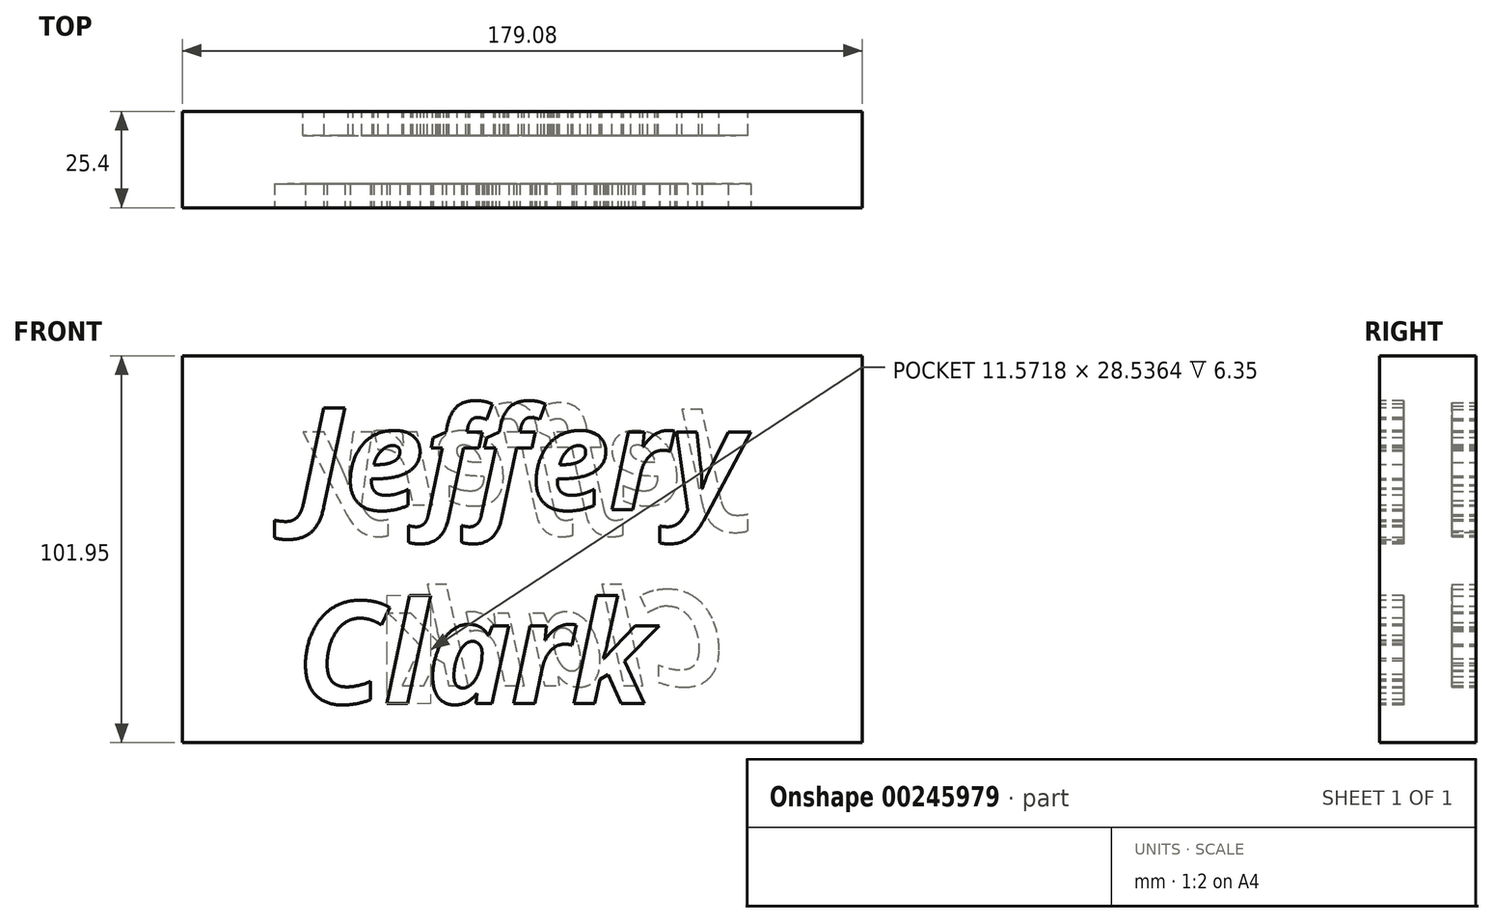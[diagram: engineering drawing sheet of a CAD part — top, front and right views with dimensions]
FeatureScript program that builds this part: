
annotation { "Feature Type Name" : "Feature", "Feature Type Description" : "" }
export const myFeature = defineFeature(function(context is Context, id is Id, definition is map)
    precondition{}
    {
        {
            var Q0;
            Q0=qCreatedBy(makeId("Front.planeOp"),FACE);
            var sketch = newSketch(context, id + "F0", { "sketchPlane" : qUnion([Q0])});
            skLineSegment(sketch, "E0.bottom", {"start": v(-67.38, 41.89) * mm, "end": v(111.7, 41.89) * mm});
            skLineSegment(sketch, "E0.top", {"start": v(-67.38, -60.06) * mm, "end": v(111.7, -60.06) * mm});
            skLineSegment(sketch, "E0.left", {"start": v(-67.38, 41.89) * mm, "end": v(-67.38, -60.06) * mm});
            skLineSegment(sketch, "E0.right", {"start": v(111.7, 41.89) * mm, "end": v(111.7, -60.06) * mm});
            skLineSegment(sketch, "E1.bottom", {"start": v(-3.55, 41.89) * mm, "end": v(-18.62, 41.89) * mm});
            skLineSegment(sketch, "E1.top", {"start": v(-3.55, 41.89) * mm, "end": v(-18.62, 41.89) * mm});
            skLineSegment(sketch, "E1.left", {"start": v(-3.55, 41.89) * mm, "end": v(-3.55, 41.89) * mm});
            skLineSegment(sketch, "E1.right", {"start": v(-18.62, 41.89) * mm, "end": v(-18.62, 41.89) * mm});
            skLineSegment(sketch, "E2.bottom", {"start": v(-67.38, 41.89) * mm, "end": v(-67.38, 41.89) * mm});
            skLineSegment(sketch, "E2.top", {"start": v(-67.38, -60.06) * mm, "end": v(-67.38, -60.06) * mm});
            skSolve(sketch);
        }
        {
            var Q0;
            Q0=makeQuery(id+"F0.imprint","IMPRINT",FACE,{"disambiguationData":[TD([[makeQuery(id+"F0.imprint","IMPRINT",EDGE,{"derivedFrom":sQuery(id+"F0.wireOp",EDGE,"E0.top")}),1.0]])]});
            extrude(context, id + "F1", {"entities" : qUnion([Q0]), "depth" : 25.4 * mm});
        }
        {
            var Q0;
            Q0=makeQuery(id+"F1.opExtrude","CAP_FACE",FACE,{"disambiguationData":[OSD([sQuery(id+"F0.wireOp",EDGE,"E0.bottom"),sQuery(id+"F0.wireOp",EDGE,"E0.top"),sQuery(id+"F0.wireOp",EDGE,"E0.right"),sQuery(id+"F0.wireOp",EDGE,"E1.top"),sQuery(id+"F0.wireOp",EDGE,"E0.left")])],"isStart":false});
            var sketch = newSketch(context, id + "F2", { "sketchPlane" : qUnion([Q0])});
            skText(sketch, "E3", { "text": "Jeffery\nClark", "fontName": "OpenSans-BoldItalic.ttf"});
            const initialGuessF2  = {"E3": [-0.03723, 0.00133, 1, 0, 0.02704]};
            skSetInitialGuess(sketch, initialGuessF2);
            skSolve(sketch);
        }
        {
            var Q0;
            Q0 = qSketchRegion(id + "F2", true);
            extrude(context, id + "F3", {"entities" : qUnion([Q0]), "operationType" : NewBodyOperationType.REMOVE, "oppositeDirection" : true, "depth" : 6.35 * mm});
        }
        {
            var Q0;
            Q0=makeQuery(id+"F1.opExtrude","CAP_FACE",FACE,{"disambiguationData":[OSD([sQuery(id+"F0.wireOp",EDGE,"E0.bottom"),sQuery(id+"F0.wireOp",EDGE,"E0.top"),sQuery(id+"F0.wireOp",EDGE,"E0.right"),sQuery(id+"F0.wireOp",EDGE,"E1.top"),sQuery(id+"F0.wireOp",EDGE,"E0.left")])],"isStart":true});
            var sketch = newSketch(context, id + "F4", { "sketchPlane" : qUnion([Q0])});
            skText(sketch, "E4", { "text": "Jeffery\nClark", "fontName": "OpenSans-BoldItalic.ttf"});
            const initialGuessF4  = {"E4": [-0.07606, 0.00266, 1, 0, 0.02527]};
            skSetInitialGuess(sketch, initialGuessF4);
            skSolve(sketch);
        }
        {
            var Q0;
            Q0 = qSketchRegion(id + "F4", true);
            extrude(context, id + "F5", {"entities" : qUnion([Q0]), "operationType" : NewBodyOperationType.REMOVE, "oppositeDirection" : true, "depth" : 6.35 * mm});
        }
    });
